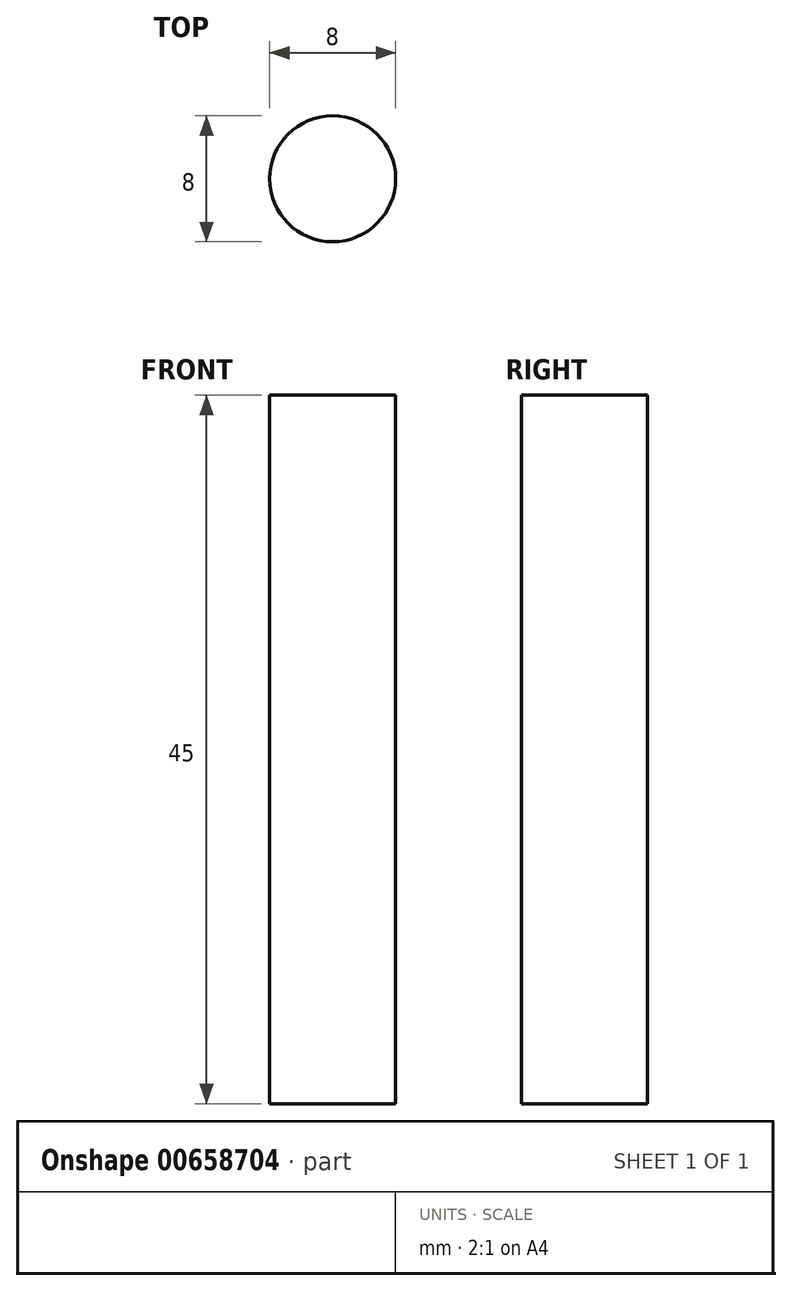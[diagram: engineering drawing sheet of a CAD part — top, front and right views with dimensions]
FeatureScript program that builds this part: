
annotation { "Feature Type Name" : "Feature", "Feature Type Description" : "" }
export const myFeature = defineFeature(function(context is Context, id is Id, definition is map)
    precondition{}
    {
        {
            var Q0;
            Q0=qCreatedBy(makeId("Top.planeOp"),FACE);
            var sketch = newSketch(context, id + "F0", { "sketchPlane" : qUnion([Q0])});
            skCircle(sketch, "E0", {"center": v(0, 0) * mm, "radius": 4 * mm});
            skSolve(sketch);
        }
        {
            var Q0;
            Q0=makeQuery(id+"F0.imprint","IMPRINT",FACE,{"disambiguationData":[TD([[makeQuery(id+"F0.imprint","IMPRINT",EDGE,{"derivedFrom":sQuery(id+"F0.wireOp",EDGE,"E0")}),1.0]])]});
            extrude(context, id + "F1", {"entities" : qUnion([Q0]), "depth" : 45 * mm, "symmetric" : true});
        }
    });
